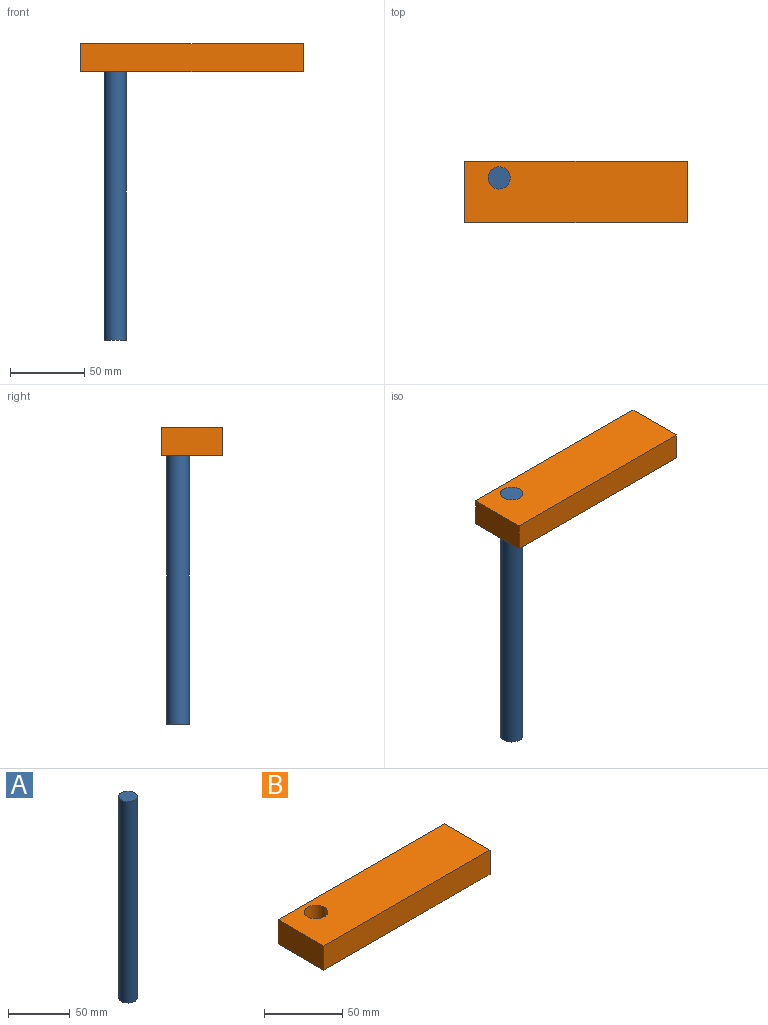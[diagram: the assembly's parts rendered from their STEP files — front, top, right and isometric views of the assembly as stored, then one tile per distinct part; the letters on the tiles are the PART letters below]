
ASSEMBLY  parts=2 mates=1
PART A: 3 faces, bbox 15x15x200 mm
  f0: cylinder r=7.5mm len=200mm, axis (0,0,1), area 9424.8mm2, adj f1,f2
  f1: plane 15x15mm, normal (0,0,-1), area 176.7mm2, adj f0
  f2: plane 15x15mm, normal (0,0,1), area 176.7mm2, adj f0
PART B: 7 faces, bbox 150x41.2x18.9 mm
  f0: plane 150x18.9mm, normal (0,1,0), area 2835mm2, adj f1,f4,f5,f6
  f1: plane 41.25x18.9mm, normal (-1,0,0), area 779.6mm2, adj f0,f2,f5,f6
  f2: plane 150x18.9mm, normal (0,-1,0), area 2835mm2, adj f1,f4,f5,f6
  f3: cylinder r=7.5mm len=18.9mm, axis (0,0,1), area 890.6mm2, adj f5,f6
  f4: plane 41.25x18.9mm, normal (1,0,0), area 779.6mm2, adj f0,f2,f5,f6
  f5: plane 150x41.25mm, normal (0,0,-1), area 6010.4mm2, adj f0,f1,f2,f3,f4
  f6: plane 150x41.25mm, normal (0,0,1), area 6010.4mm2, adj f0,f1,f2,f3,f4
PLACE A t=(21.51,76.76,13.16)mm
PLACE B t=(-1.58,7.86,13.16)mm
MATE fastened A.f0 <-> B.f3  axis (0,0,1) through (-28.21,47.96,13.16)mm
